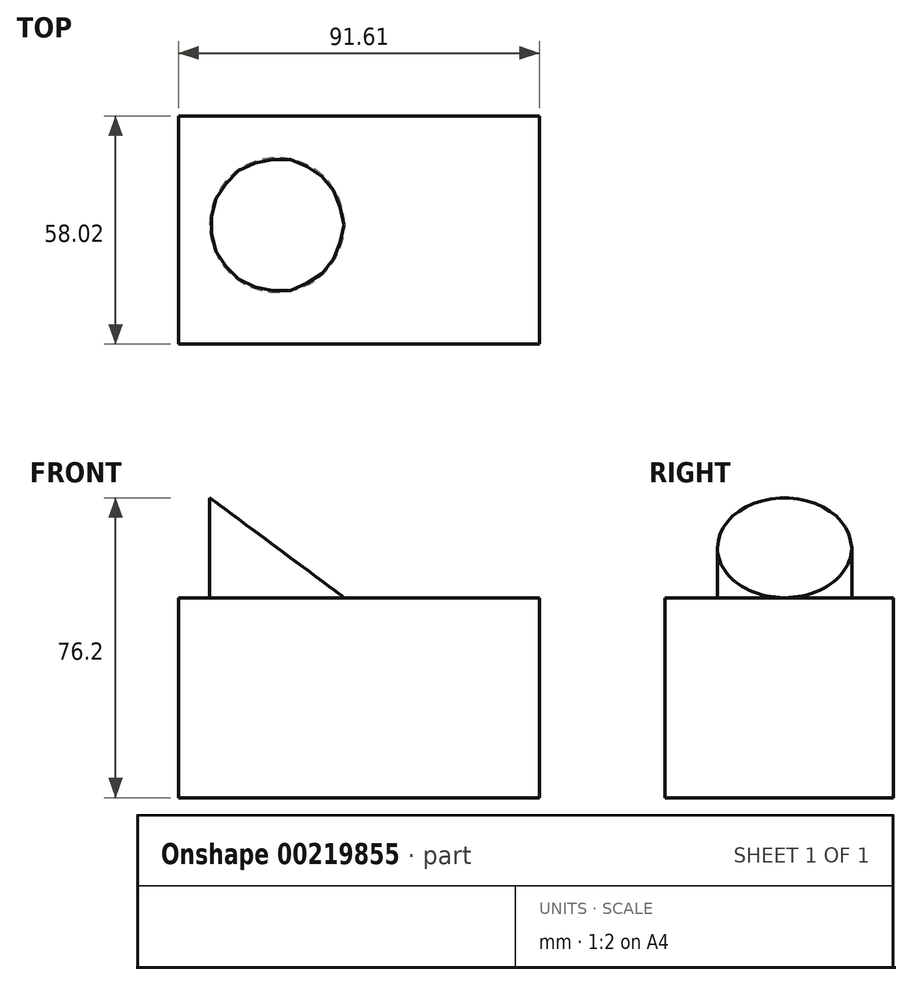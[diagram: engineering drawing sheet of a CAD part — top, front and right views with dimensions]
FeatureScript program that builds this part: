
annotation { "Feature Type Name" : "Feature", "Feature Type Description" : "" }
export const myFeature = defineFeature(function(context is Context, id is Id, definition is map)
    precondition{}
    {
        {
            var Q0;
            Q0=qCreatedBy(makeId("Top.planeOp"),FACE);
            var sketch = newSketch(context, id + "F0", { "sketchPlane" : qUnion([Q0])});
            skLineSegment(sketch, "E0.bottom", {"start": v(-69.63, 71.23) * mm, "end": v(21.98, 71.23) * mm});
            skLineSegment(sketch, "E0.top", {"start": v(-69.63, 13.21) * mm, "end": v(21.98, 13.21) * mm});
            skLineSegment(sketch, "E0.left", {"start": v(-69.63, 71.23) * mm, "end": v(-69.63, 13.21) * mm});
            skLineSegment(sketch, "E0.right", {"start": v(21.98, 71.23) * mm, "end": v(21.98, 13.21) * mm});
            skSolve(sketch);
        }
        {
            var Q0;
            Q0 = qSketchRegion(id + "F0", true);
            extrude(context, id + "F1", {"entities" : qUnion([Q0]), "depth" : 50.8 * mm});
        }
        {
            var Q0;
            Q0=makeQuery(id+"F1.opExtrude","CAP_FACE",FACE,{"disambiguationData":[OSD([sQuery(id+"F0.wireOp",EDGE,"E0.bottom"),sQuery(id+"F0.wireOp",EDGE,"E0.top"),sQuery(id+"F0.wireOp",EDGE,"E0.left"),sQuery(id+"F0.wireOp",EDGE,"E0.right")])],"isStart":false});
            var sketch = newSketch(context, id + "F2", { "sketchPlane" : qUnion([Q0])});
            skCircle(sketch, "E1", {"center": v(-44.65, 43.51) * mm, "radius": 17.08 * mm});
            skSolve(sketch);
        }
        {
            var Q0;
            Q0=makeQuery(id+"F2.imprint","IMPRINT",FACE,{"disambiguationData":[TD([[makeQuery(id+"F2.imprint","IMPRINT",EDGE,{"derivedFrom":sQuery(id+"F2.wireOp",EDGE,"E1")}),1.0]])]});
            extrude(context, id + "F3", {"entities" : qUnion([Q0]), "operationType" : NewBodyOperationType.ADD, "depth" : 25.4 * mm});
        }
        {
            var Q0;
            Q0=makeQuery(id+"F1.opExtrude","CAP_FACE",FACE,{"disambiguationData":[OSD([sQuery(id+"F0.wireOp",EDGE,"E0.bottom"),sQuery(id+"F0.wireOp",EDGE,"E0.top"),sQuery(id+"F0.wireOp",EDGE,"E0.left"),sQuery(id+"F0.wireOp",EDGE,"E0.right")])],"isStart":false});
            extrude(context, id + "F4", {"entities" : qUnion([Q0]), "operationType" : NewBodyOperationType.ADD, "oppositeDirection" : true, "depth" : 50.8 * mm});
        }
        {
            var Q0;
            Q0=makeQuery(id+"F1.opExtrude","SWEPT_FACE",FACE,{"disambiguationData":[OSD([sQuery(id+"F0.wireOp",EDGE,"E0.top")])]});
            var sketch = newSketch(context, id + "F5", { "sketchPlane" : qUnion([Q0])});
            skLineSegment(sketch, "E2.0", {"start": v(-61.72, 76.2) * mm, "end": v(-27.57, 76.2) * mm});
            skLineSegment(sketch, "E3", {"start": v(-27.57, 76.2) * mm, "end": v(-27.57, 50.8) * mm});
            skLineSegment(sketch, "E4", {"start": v(-61.72, 76.2) * mm, "end": v(-27.57, 50.8) * mm});
            skSolve(sketch);
        }
        {
            var Q0;
            Q0 = qSketchRegion(id + "F5", true);
            extrude(context, id + "F6", {"entities" : qUnion([Q0]), "operationType" : NewBodyOperationType.REMOVE, "endBound" : BoundingType.THROUGH_ALL, "oppositeDirection" : true, "depth" : 25.4 * mm});
        }
    });
